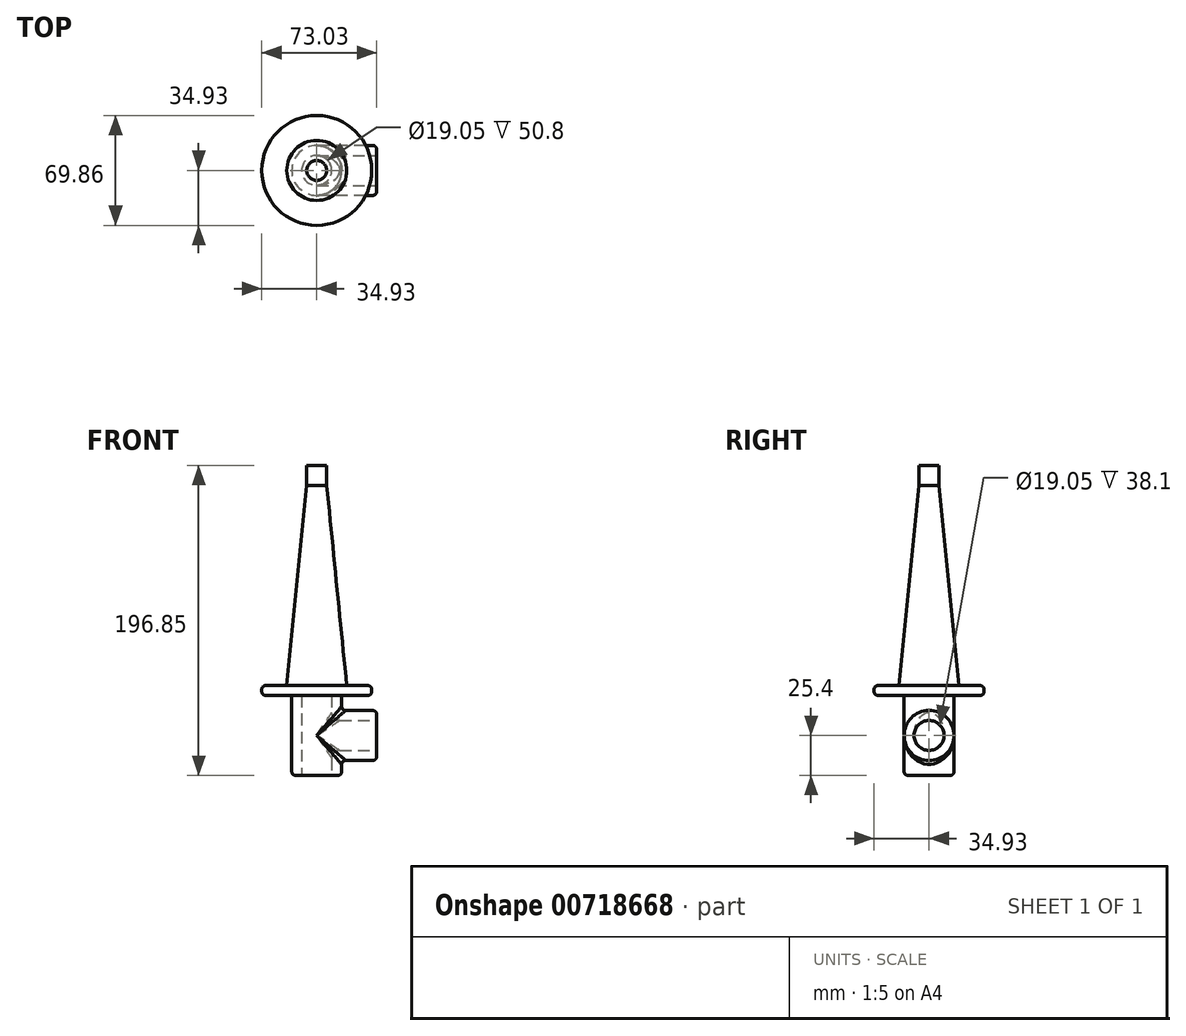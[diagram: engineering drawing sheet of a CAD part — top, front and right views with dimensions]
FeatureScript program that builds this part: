
annotation { "Feature Type Name" : "Feature", "Feature Type Description" : "" }
export const myFeature = defineFeature(function(context is Context, id is Id, definition is map)
    precondition{}
    {
        {
            var Q0;
            Q0=qCreatedBy(makeId("Top.planeOp"),FACE);
            var sketch = newSketch(context, id + "F0", { "sketchPlane" : qUnion([Q0])});
            skCircle(sketch, "E0", {"center": v(0, 0) * mm, "radius": 19.05 * mm});
            skSolve(sketch);
        }
        {
            var Q0;
            Q0=qCreatedBy(makeId("Top.planeOp"),FACE);
            cPlane(context, id + "F1", {"entities" : qUnion([Q0]), "cplaneType" : CPlaneType.OFFSET, "offset" : 127 * mm, "width" : 152.4 * mm, "height" : 152.4 * mm});
        }
        {
            var Q0;
            Q0=qCreatedBy(id+"F1.planeOp",FACE);
            var sketch = newSketch(context, id + "F2", { "sketchPlane" : qUnion([Q0])});
            skCircle(sketch, "E1", {"center": v(0, 0) * mm, "radius": 6.35 * mm});
            skSolve(sketch);
        }
        {
            var Q0;
            Q0=makeQuery(id+"F0.imprint","IMPRINT",FACE,{"disambiguationData":[TD([[makeQuery(id+"F0.imprint","IMPRINT",EDGE,{"derivedFrom":sQuery(id+"F0.wireOp",EDGE,"E0")}),1.0]])]});
            var Q1;
            Q1=makeQuery(id+"F2.imprint","IMPRINT",FACE,{"disambiguationData":[TD([[makeQuery(id+"F2.imprint","IMPRINT",EDGE,{"derivedFrom":sQuery(id+"F2.wireOp",EDGE,"E1")}),1.0]])]});
            loft(context, id + "F3", {"sheetProfilesArray" : [{ "sheetProfileEntities" : qUnion([Q0]) }, { "sheetProfileEntities" : qUnion([Q1]) }]});
        }
        {
            var Q0;
            Q0=qCreatedBy(makeId("Top.planeOp"),FACE);
            var sketch = newSketch(context, id + "F4", { "sketchPlane" : qUnion([Q0])});
            skCircle(sketch, "E2", {"center": v(0, 0) * mm, "radius": 34.93 * mm});
            skSolve(sketch);
        }
        {
            var Q0;
            Q0=makeQuery(id+"F4.imprint","IMPRINT",FACE,{"disambiguationData":[TD([[makeQuery(id+"F4.imprint","IMPRINT",EDGE,{"derivedFrom":sQuery(id+"F4.wireOp",EDGE,"E2")}),1.0]])]});
            extrude(context, id + "F5", {"entities" : qUnion([Q0]), "operationType" : NewBodyOperationType.ADD, "oppositeDirection" : true, "depth" : 6.35 * mm, "offsetDistance" : 25.4 * mm});
        }
        {
            var Q0;
            Q0=makeQuery(id+"F5.opExtrude","CAP_FACE",FACE,{"disambiguationData":[OSD([sQuery(id+"F4.wireOp",EDGE,"E2")])],"isStart":false});
            var sketch = newSketch(context, id + "F6", { "sketchPlane" : qUnion([Q0])});
            skCircle(sketch, "E3", {"center": v(0, 0) * mm, "radius": 15.88 * mm});
            skSolve(sketch);
        }
        {
            var Q0;
            Q0=makeQuery(id+"F6.imprint","IMPRINT",FACE,{"disambiguationData":[TD([[makeQuery(id+"F6.imprint","IMPRINT",EDGE,{"derivedFrom":sQuery(id+"F6.wireOp",EDGE,"E3")}),1.0]])]});
            extrude(context, id + "F7", {"entities" : qUnion([Q0]), "operationType" : NewBodyOperationType.ADD, "depth" : 50.8 * mm, "offsetDistance" : 25.4 * mm});
        }
        {
            var Q0;
            Q0=qCreatedBy(makeId("Right.planeOp"),FACE);
            var sketch = newSketch(context, id + "F8", { "sketchPlane" : qUnion([Q0])});
            skCircle(sketch, "E4", {"center": v(0, -31.75) * mm, "radius": 15.88 * mm});
            skSolve(sketch);
        }
        {
            var Q0;
            Q0 = qSketchRegion(id + "F8", true);
            extrude(context, id + "F9", {"entities" : qUnion([Q0]), "operationType" : NewBodyOperationType.ADD, "depth" : 38.1 * mm, "offsetDistance" : 25.4 * mm});
        }
        {
            var Q0;
            Q0=makeQuery(id+"F9.opExtrude","CAP_FACE",FACE,{"disambiguationData":[OSD([sQuery(id+"F8.wireOp",EDGE,"E4")])],"isStart":false});
            var sketch = newSketch(context, id + "F10", { "sketchPlane" : qUnion([Q0])});
            skCircle(sketch, "E5", {"center": v(0, -31.75) * mm, "radius": 9.53 * mm});
            skSolve(sketch);
        }
        {
            var Q0;
            Q0=makeQuery(id+"F10.imprint","IMPRINT",FACE,{"disambiguationData":[TD([[makeQuery(id+"F10.imprint","IMPRINT",EDGE,{"derivedFrom":sQuery(id+"F10.wireOp",EDGE,"E5")}),1.0]])]});
            extrude(context, id + "F11", {"entities" : qUnion([Q0]), "operationType" : NewBodyOperationType.REMOVE, "oppositeDirection" : true, "depth" : 38.1 * mm, "offsetDistance" : 25.4 * mm});
        }
        {
            var Q0;
            Q0=makeQuery(id+"F7.opExtrude","CAP_FACE",FACE,{"disambiguationData":[OSD([sQuery(id+"F6.wireOp",EDGE,"E3")])],"isStart":false});
            var sketch = newSketch(context, id + "F12", { "sketchPlane" : qUnion([Q0])});
            skCircle(sketch, "E6", {"center": v(0, 0) * mm, "radius": 9.53 * mm});
            skSolve(sketch);
        }
        {
            var Q0;
            Q0=makeQuery(id+"F12.imprint","IMPRINT",FACE,{"disambiguationData":[TD([[makeQuery(id+"F12.imprint","IMPRINT",EDGE,{"derivedFrom":sQuery(id+"F12.wireOp",EDGE,"E6")}),1.0]])]});
            extrude(context, id + "F13", {"entities" : qUnion([Q0]), "operationType" : NewBodyOperationType.REMOVE, "oppositeDirection" : true, "depth" : 50.8 * mm, "offsetDistance" : 25.4 * mm});
        }
        {
            var Q0;
            Q0=makeQuery(id+"F5.opExtrude","CAP_EDGE",EDGE,{"disambiguationData":[OSD([sQuery(id+"F4.wireOp",EDGE,"E2")])],"isStart":true});
            var Q1;
            Q1=makeQuery(id+"F5.opExtrude","CAP_EDGE",EDGE,{"disambiguationData":[OSD([sQuery(id+"F4.wireOp",EDGE,"E2")])],"isStart":false});
            var Q2;
            Q2=makeQuery(id+"F7.opExtrude","CAP_EDGE",EDGE,{"disambiguationData":[OSD([sQuery(id+"F6.wireOp",EDGE,"E3")])],"isStart":false});
            var Q3;
            Q3=makeQuery(id+"F9.opExtrude","CAP_EDGE",EDGE,{"disambiguationData":[OSD([sQuery(id+"F8.wireOp",EDGE,"E4")])],"isStart":false});
            var Q4;
            Q4=makeQuery(id+"F9.boolean.opBoolean","INTERSECT",EDGE,{"disambiguationData":[OD(0.0)],"derivedFrom":[makeQuery(id+"F7.opExtrude","SWEPT_FACE",FACE,{"disambiguationData":[OSD([sQuery(id+"F6.wireOp",EDGE,"E3")])]}),makeQuery(id+"F9.opExtrude","SWEPT_FACE",FACE,{"disambiguationData":[OSD([sQuery(id+"F8.wireOp",EDGE,"E4")])]})]});
            var Q5;
            Q5=makeQuery(id+"F9.boolean.opBoolean","INTERSECT",EDGE,{"disambiguationData":[OD(1.0)],"derivedFrom":[makeQuery(id+"F7.opExtrude","SWEPT_FACE",FACE,{"disambiguationData":[OSD([sQuery(id+"F6.wireOp",EDGE,"E3")])]}),makeQuery(id+"F9.opExtrude","SWEPT_FACE",FACE,{"disambiguationData":[OSD([sQuery(id+"F8.wireOp",EDGE,"E4")])]})]});
            var Q6;
            Q6=makeQuery(id+"F13.boolean.opBoolean","COPY",EDGE,{"derivedFrom":makeQuery(id+"F13.opExtrude","CAP_EDGE",EDGE,{"disambiguationData":[OSD([sQuery(id+"F12.wireOp",EDGE,"E6")])],"isStart":true})});
            var Q7;
            Q7=makeQuery(id+"F11.boolean.opBoolean","COPY",EDGE,{"derivedFrom":makeQuery(id+"F11.opExtrude","CAP_EDGE",EDGE,{"disambiguationData":[OSD([sQuery(id+"F10.wireOp",EDGE,"E5")])],"isStart":true})});
            var Q8;
            Q8=makeQuery(id+"F7.opExtrude","CAP_EDGE",EDGE,{"disambiguationData":[OSD([sQuery(id+"F6.wireOp",EDGE,"E3")])],"isStart":true});
            fillet(context, id + "F14", {"entities" : qUnion([Q0, Q1, Q2, Q3, Q4, Q5, Q6, Q7, Q8]), "radius" : 2.54 * mm, "tangentPropagation" : true, "allowEdgeOverflow" : false});
        }
        {
            var Q0;
            Q0=makeQuery(id+"F13.boolean.opBoolean","INTERSECT",EDGE,{"disambiguationData":[OD(1.0)],"derivedFrom":[makeQuery(id+"F11.boolean.opBoolean","COPY",FACE,{"derivedFrom":makeQuery(id+"F11.opExtrude","SWEPT_FACE",FACE,{"disambiguationData":[OSD([sQuery(id+"F10.wireOp",EDGE,"E5")])]})}),makeQuery(id+"F13.opExtrude","SWEPT_FACE",FACE,{"disambiguationData":[OSD([sQuery(id+"F12.wireOp",EDGE,"E6")])]})]});
            var Q1;
            Q1=makeQuery(id+"F13.boolean.opBoolean","INTERSECT",EDGE,{"disambiguationData":[OD(0.0)],"derivedFrom":[makeQuery(id+"F11.boolean.opBoolean","COPY",FACE,{"derivedFrom":makeQuery(id+"F11.opExtrude","SWEPT_FACE",FACE,{"disambiguationData":[OSD([sQuery(id+"F10.wireOp",EDGE,"E5")])]})}),makeQuery(id+"F13.opExtrude","SWEPT_FACE",FACE,{"disambiguationData":[OSD([sQuery(id+"F12.wireOp",EDGE,"E6")])]})]});
            fillet(context, id + "F15", {"entities" : qUnion([Q0, Q1]), "radius" : 5.08 * mm, "tangentPropagation" : true, "allowEdgeOverflow" : false});
        }
        {
            var Q0;
            Q0=makeQuery(id+"F3.opLoft","CAP_FACE",FACE,{"disambiguationData":[OSD([makeQuery(id+"F2.imprint","IMPRINT",FACE,{"disambiguationData":[TD([[makeQuery(id+"F2.imprint","IMPRINT",EDGE,{"derivedFrom":sQuery(id+"F2.wireOp",EDGE,"E1")}),1.0]])]})])],"isStart":true});
            extrude(context, id + "F16", {"entities" : qUnion([Q0]), "operationType" : NewBodyOperationType.ADD, "depth" : 12.7 * mm, "offsetDistance" : 25.4 * mm});
        }
    });
